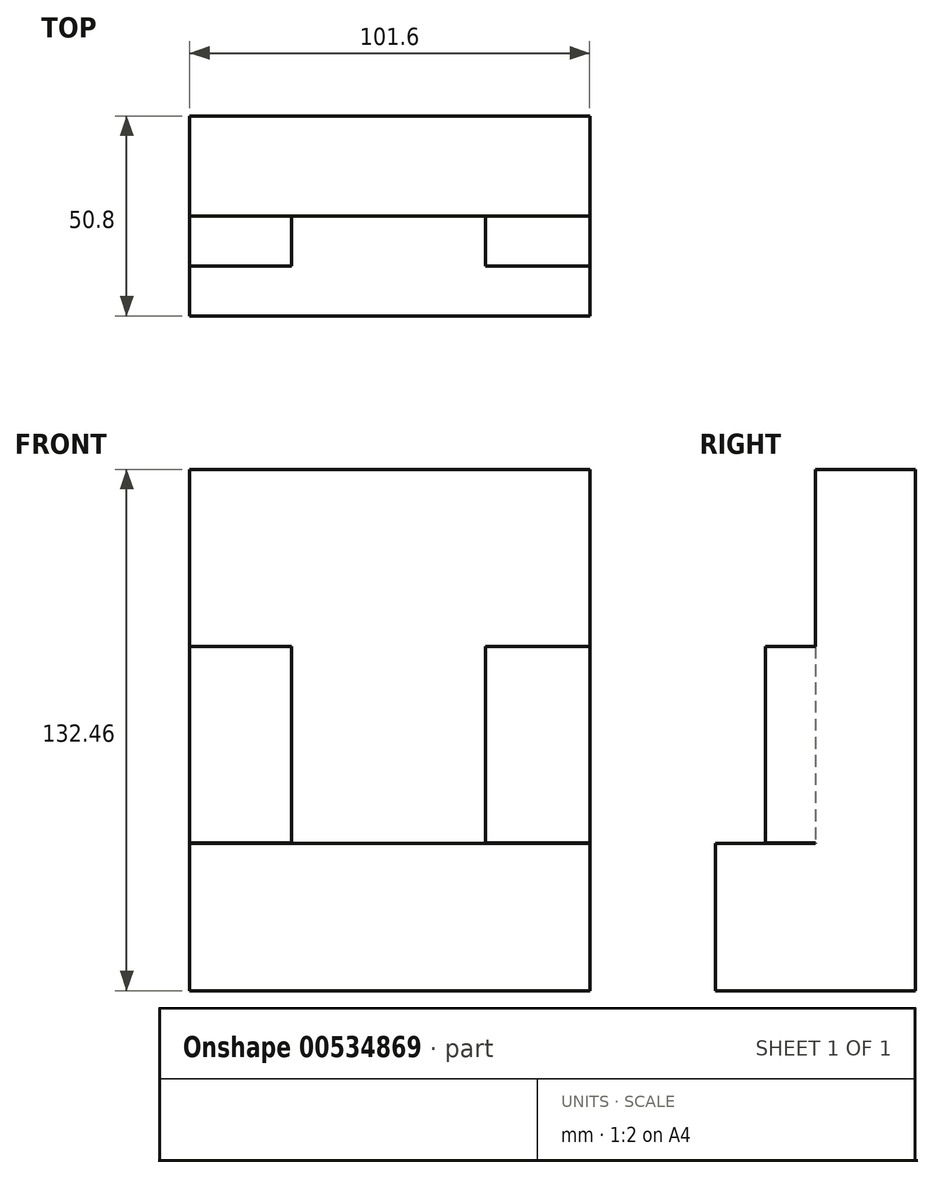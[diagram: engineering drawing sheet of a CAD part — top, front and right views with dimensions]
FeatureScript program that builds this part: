
annotation { "Feature Type Name" : "Feature", "Feature Type Description" : "" }
export const myFeature = defineFeature(function(context is Context, id is Id, definition is map)
    precondition{}
    {
        {
            var Q0;
            Q0=qCreatedBy(makeId("Front.planeOp"),FACE);
            var sketch = newSketch(context, id + "F0", { "sketchPlane" : qUnion([Q0])});
            skLineSegment(sketch, "E0.bottom", {"start": v(-49.96, 66.65) * mm, "end": v(51.64, 66.65) * mm});
            skLineSegment(sketch, "E0.top", {"start": v(-49.96, -65.8) * mm, "end": v(51.64, -65.8) * mm});
            skLineSegment(sketch, "E0.left", {"start": v(-49.96, 66.65) * mm, "end": v(-49.96, -65.8) * mm});
            skLineSegment(sketch, "E0.right", {"start": v(51.64, 66.65) * mm, "end": v(51.64, -65.8) * mm});
            skLineSegment(sketch, "E1.bottom", {"start": v(-49.96, -28.67) * mm, "end": v(51.64, -28.67) * mm});
            skLineSegment(sketch, "E1.left", {"start": v(-49.96, -28.67) * mm, "end": v(-49.96, -65.8) * mm});
            skLineSegment(sketch, "E1.right", {"start": v(51.64, -28.67) * mm, "end": v(51.64, -65.8) * mm});
            skLineSegment(sketch, "E2.bottom", {"start": v(-49.96, 22.76) * mm, "end": v(-28.88, 22.76) * mm});
            skLineSegment(sketch, "E2.top", {"start": v(-49.96, -28.67) * mm, "end": v(-28.88, -28.67) * mm});
            skLineSegment(sketch, "E2.left", {"start": v(-49.96, 22.76) * mm, "end": v(-49.96, -28.67) * mm});
            skLineSegment(sketch, "E2.right", {"start": v(-28.88, 22.76) * mm, "end": v(-28.88, -28.67) * mm});
            skLineSegment(sketch, "E3.bottom", {"start": v(30.56, 22.76) * mm, "end": v(51.64, 22.76) * mm});
            skLineSegment(sketch, "E3.top", {"start": v(30.56, -28.67) * mm, "end": v(51.64, -28.67) * mm});
            skLineSegment(sketch, "E3.left", {"start": v(30.56, 22.76) * mm, "end": v(30.56, -28.67) * mm});
            skLineSegment(sketch, "E3.right", {"start": v(51.64, 22.76) * mm, "end": v(51.64, -28.67) * mm});
            skSolve(sketch);
        }
        {
            var Q0;
            Q0=makeQuery(id+"F0.imprint","IMPRINT",FACE,{"disambiguationData":[TD([[makeQuery(id+"F0.imprint","IMPRINT",EDGE,{"derivedFrom":sQuery(id+"F0.wireOp",EDGE,"E2.bottom")}),-1.0]])]});
            var Q1;
            Q1=makeQuery(id+"F0.imprint","IMPRINT",FACE,{"disambiguationData":[TD([[makeQuery(id+"F0.imprint","IMPRINT",EDGE,{"derivedFrom":sQuery(id+"F0.wireOp",EDGE,"E3.bottom")}),-1.0]])]});
            var Q2;
            Q2=makeQuery(id+"F0.imprint","IMPRINT",FACE,{"disambiguationData":[TD([[makeQuery(id+"F0.imprint","IMPRINT",EDGE,{"derivedFrom":sQuery(id+"F0.wireOp",EDGE,"E0.bottom")}),-1.0]])]});
            var Q3;
            Q3=makeQuery(id+"F0.imprint","IMPRINT",FACE,{"disambiguationData":[TD([[makeQuery(id+"F0.imprint","IMPRINT",EDGE,{"derivedFrom":sQuery(id+"F0.wireOp",EDGE,"E1.bottom")}),-1.0]])]});
            extrude(context, id + "F1", {"entities" : qUnion([Q0, Q1, Q2, Q3]), "oppositeDirection" : true, "depth" : 50.8 * mm, "offsetDistance" : 25.4 * mm});
        }
        {
            var Q0;
            Q0=qCreatedBy(makeId("Front.planeOp"),FACE);
            var sketch = newSketch(context, id + "F2", { "sketchPlane" : qUnion([Q0])});
            skLineSegment(sketch, "E4.bottom", {"start": v(-50.15, -28.2) * mm, "end": v(51.64, -28.2) * mm});
            skLineSegment(sketch, "E4.top", {"start": v(-50.15, -65.68) * mm, "end": v(51.64, -65.68) * mm});
            skLineSegment(sketch, "E4.left", {"start": v(-50.15, -28.2) * mm, "end": v(-50.15, -65.68) * mm});
            skLineSegment(sketch, "E4.right", {"start": v(51.64, -28.2) * mm, "end": v(51.64, -65.68) * mm});
            skLineSegment(sketch, "E5.bottom", {"start": v(-50.49, 21.65) * mm, "end": v(-24.05, 21.65) * mm});
            skLineSegment(sketch, "E5.top", {"start": v(-50.49, -28.2) * mm, "end": v(-24.05, -28.2) * mm});
            skLineSegment(sketch, "E5.left", {"start": v(-50.49, 21.65) * mm, "end": v(-50.49, -28.2) * mm});
            skLineSegment(sketch, "E5.right", {"start": v(-24.05, 21.65) * mm, "end": v(-24.05, -28.2) * mm});
            skLineSegment(sketch, "E6.bottom", {"start": v(25.21, 21.65) * mm, "end": v(51.64, 21.65) * mm});
            skLineSegment(sketch, "E6.top", {"start": v(25.21, -28.2) * mm, "end": v(51.64, -28.2) * mm});
            skLineSegment(sketch, "E6.left", {"start": v(25.21, 21.65) * mm, "end": v(25.21, -28.2) * mm});
            skLineSegment(sketch, "E6.right", {"start": v(51.64, 21.65) * mm, "end": v(51.64, -28.2) * mm});
            skSolve(sketch);
        }
        {
            var Q0;
            Q0=makeQuery(id+"F2.imprint","IMPRINT",FACE,{"disambiguationData":[TD([[makeQuery(id+"F2.imprint","IMPRINT",EDGE,{"derivedFrom":sQuery(id+"F2.wireOp",EDGE,"E6.bottom")}),-1.0]])]});
            var Q1;
            Q1=makeQuery(id+"F2.imprint","IMPRINT",FACE,{"disambiguationData":[TD([[makeQuery(id+"F2.imprint","IMPRINT",EDGE,{"derivedFrom":sQuery(id+"F2.wireOp",EDGE,"E5.bottom")}),-1.0]])]});
            extrude(context, id + "F3", {"entities" : qUnion([Q0, Q1]), "operationType" : NewBodyOperationType.REMOVE, "oppositeDirection" : true, "depth" : 12.7 * mm, "offsetDistance" : 25.4 * mm});
        }
        {
            var Q0;
            Q0=qCreatedBy(makeId("Front.planeOp"),FACE);
            var sketch = newSketch(context, id + "F4", { "sketchPlane" : qUnion([Q0])});
            skLineSegment(sketch, "E7.bottom", {"start": v(-50.7, -28.42) * mm, "end": v(51.88, -28.42) * mm});
            skLineSegment(sketch, "E7.top", {"start": v(-50.7, -66.16) * mm, "end": v(51.88, -66.16) * mm});
            skLineSegment(sketch, "E7.left", {"start": v(-50.7, -28.42) * mm, "end": v(-50.7, -66.16) * mm});
            skLineSegment(sketch, "E7.right", {"start": v(51.88, -28.42) * mm, "end": v(51.88, -66.16) * mm});
            skSolve(sketch);
        }
        {
            var Q0;
            Q0=makeQuery(id+"F4.imprint","IMPRINT",FACE,{"disambiguationData":[TD([[makeQuery(id+"F4.imprint","IMPRINT",EDGE,{"derivedFrom":sQuery(id+"F4.wireOp",EDGE,"E7.bottom")}),-1.0]])]});
            extrude(context, id + "F5", {"entities" : qUnion([Q0]), "operationType" : NewBodyOperationType.ADD, "depth" : 25.4 * mm, "offsetDistance" : 25.4 * mm});
        }
        {
            var Q0;
            Q0=makeQuery(id+"F1.opExtrude","CAP_FACE",FACE,{"disambiguationData":[OSD([sQuery(id+"F0.wireOp",EDGE,"E0.bottom"),sQuery(id+"F0.wireOp",EDGE,"E0.left"),sQuery(id+"F0.wireOp",EDGE,"E0.right"),sQuery(id+"F0.wireOp",EDGE,"E0.top"),sQuery(id+"F0.wireOp",EDGE,"E1.left"),sQuery(id+"F0.wireOp",EDGE,"E1.right"),sQuery(id+"F0.wireOp",EDGE,"E2.left"),sQuery(id+"F0.wireOp",EDGE,"E3.right")])],"isStart":true});
            extrude(context, id + "F6", {"entities" : qUnion([Q0]), "operationType" : NewBodyOperationType.REMOVE, "oppositeDirection" : true, "depth" : 25.4 * mm, "offsetDistance" : 25.4 * mm});
        }
        {
            var Q0;
            Q0=makeQuery(id+"F5.opExtrude","CAP_FACE",FACE,{"disambiguationData":[OSD([sQuery(id+"F4.wireOp",EDGE,"E7.bottom"),sQuery(id+"F4.wireOp",EDGE,"E7.top"),sQuery(id+"F4.wireOp",EDGE,"E7.left"),sQuery(id+"F4.wireOp",EDGE,"E7.right")])],"isStart":false});
            extrude(context, id + "F7", {"entities" : qUnion([Q0]), "operationType" : NewBodyOperationType.REMOVE, "oppositeDirection" : true, "depth" : 25.4 * mm, "offsetDistance" : 25.4 * mm});
        }
    });
